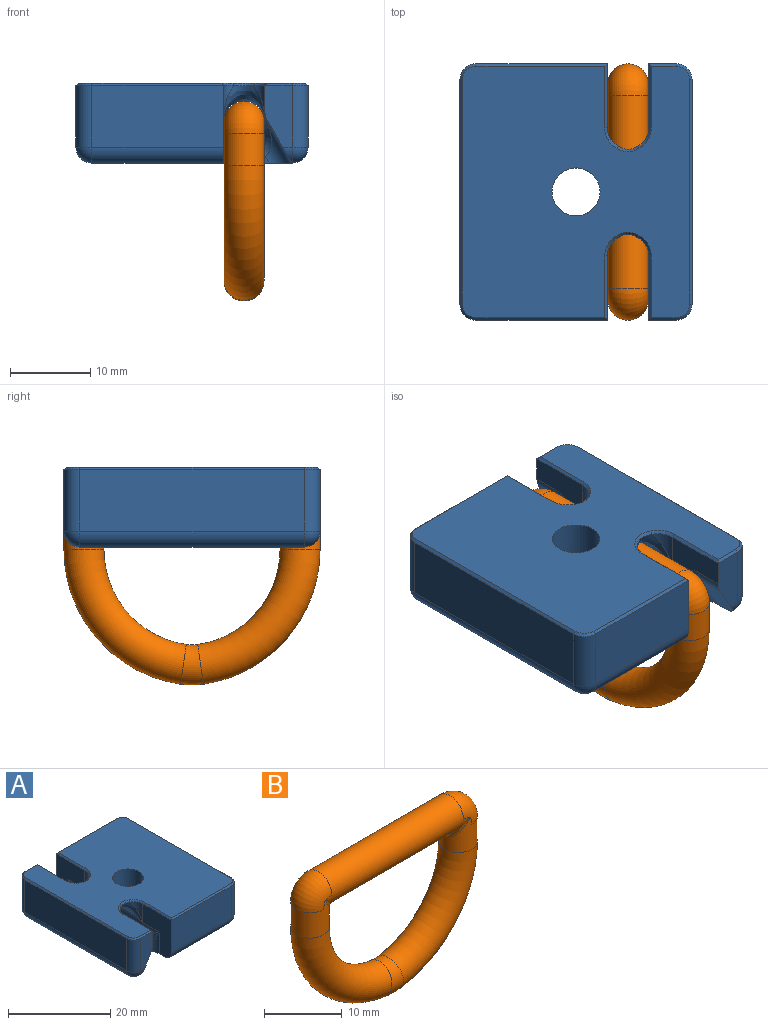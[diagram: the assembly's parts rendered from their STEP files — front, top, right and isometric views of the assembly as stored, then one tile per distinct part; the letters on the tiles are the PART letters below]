
ASSEMBLY  parts=2 mates=1
PART A: 73 faces, bbox 29.6x32.6x13.1 mm
  f0: cylinder r=2.6mm len=4.5mm, axis (0,0,1), area 6.3mm2, adj f31,f52,f54
  f1: cylinder r=2.6mm len=4.5mm, axis (0,0,1), area 6.3mm2, adj f27,f51,f71
  f2: cylinder r=2.6mm len=25mm, axis (0,-1,0), area 221.5mm2, adj f25,f27,f30,f31,f41,f42,f43,f46
  f3: plane 31.46x28.46mm, normal (0,0,1), area 745mm2, adj f33,f53,f54,f55,f56,f57,f58,f59
  f4: plane 16.4x7.7mm, normal (0,-1,0), area 126.3mm2, adj f17,f18,f30,f62
  f5: cylinder r=2mm len=1.99mm, axis (1,0,0), area 1.7mm2, adj f12,f14,f32
  f6: plane 16.4x7.7mm, normal (0,1,0), area 126.3mm2, adj f9,f24,f27,f70
  f7: plane 7.7x3.4mm, normal (0,1,0), area 21.8mm2, adj f15,f21,f25,f28,f45,f63
  f8: plane 28.61x25.61mm, normal (0,0,-1), area 558.4mm2, adj f9,f16,f17,f22,f26,f27,f29,f30
  f9: cylinder r=2mm len=16.4mm, axis (-1,0,0), area 51.5mm2, adj f6,f8,f23,f27
  f10: plane 28x7.7mm, normal (1,0,0), area 215.6mm2, adj f18,f22,f24,f66
  f11: plane 28x7.7mm, normal (-1,0,0), area 215.6mm2, adj f13,f15,f16,f59
  f12: plane 7.7x3.4mm, normal (0,-1,0), area 21.8mm2, adj f5,f13,f31,f32,f50,f55
  f13: cylinder r=2mm len=7.7mm, axis (0,0,1), area 24.2mm2, adj f11,f12,f14,f57
  f14: sphere r=2mm, area 6.3mm2, adj f5,f13,f16,f32
  f15: cylinder r=2mm len=7.7mm, axis (0,0,-1), area 24.2mm2, adj f7,f11,f19,f61
  f16: cylinder r=2mm len=28mm, axis (0,-1,0), area 88mm2, adj f8,f11,f14,f19,f28,f32
  f17: cylinder r=2mm len=16.4mm, axis (1,0,0), area 51.5mm2, adj f4,f8,f20,f30
  f18: cylinder r=2mm len=7.7mm, axis (0,0,-1), area 24.2mm2, adj f4,f10,f20,f64
  f19: sphere r=2mm, area 6.3mm2, adj f15,f16,f21,f28
  f20: sphere r=2mm, area 8.6mm2, adj f17,f18,f22
  f21: cylinder r=2mm len=1.99mm, axis (-1,0,0), area 1.7mm2, adj f7,f19,f28
  f22: cylinder r=2mm len=28mm, axis (0,1,0), area 88mm2, adj f8,f10,f20,f23
  f23: sphere r=2mm, area 4mm2, adj f9,f22,f24
  f24: cylinder r=2mm len=7.7mm, axis (0,0,1), area 24.2mm2, adj f6,f10,f23,f68
  f25: plane 8x4.5mm, normal (1,0,0), area 28.9mm2, adj f2,f7,f36,f44,f45,f65
  f26: plane 3.22x0.83mm, normal (0,1,0), area 1.1mm2, adj f8,f39,f40,f42
  f27: plane 9.7x8mm, normal (-1,0,0), area 53.3mm2, adj f1,f2,f6,f8,f9,f39,f72
  f28: plane 5.73x3.92mm, normal (0.87,0,-0.5), area 20.5mm2, adj f7,f16,f19,f21,f40,f45
  f29: plane 3.22x0.83mm, normal (0,-1,0), area 1.1mm2, adj f8,f37,f38,f47
  f30: plane 9.7x8mm, normal (-1,0,0), area 53.3mm2, adj f2,f4,f8,f17,f35,f37,f60
  f31: plane 8x4.5mm, normal (1,0,0), area 28.9mm2, adj f0,f2,f12,f49,f50,f53
  f32: plane 5.73x3.92mm, normal (0.87,0,-0.5), area 20.5mm2, adj f5,f12,f14,f16,f38,f50
  f33: cylinder r=3mm len=8mm, axis (0,0,-1), area 150.8mm2, adj f3,f34
  f34: cone r=3mm half-angle=45deg, axis (0,0,-1), area 71.1mm2, adj f8,f33
  f35: cylinder r=2.6mm len=4.5mm, axis (0,0,1), area 6.3mm2, adj f30,f52,f58
  f36: cylinder r=2.6mm len=4.5mm, axis (0,0,1), area 6.3mm2, adj f25,f51,f67
  f37: cylinder r=2.5mm len=5.2mm, axis (0,0,-1), area 7.7mm2, adj f8,f29,f30,f46
  f38: cylinder r=2.5mm len=6.57mm, axis (0.5,0,0.87), area 14.1mm2, adj f8,f29,f32,f48,f49
  f39: cylinder r=2.5mm len=5.2mm, axis (0,0,-1), area 7.7mm2, adj f8,f26,f27,f41
  f40: cylinder r=2.5mm len=6.57mm, axis (0.5,0,0.87), area 14.1mm2, adj f8,f26,f28,f43,f44
  f41: bspline ~5.1x5mm, area 7.2mm2, adj f2,f39,f42
  f42: torus R=5.1mm, axis (0,-1,0), area 7.8mm2, adj f2,f26,f41,f43
  f43: bspline ~5.32x4.45mm, area 9.5mm2, adj f2,f40,f42,f44
  f44: bspline ~2.52x2.45mm, area 3.5mm2, adj f25,f40,f43,f45
  f45: cylinder r=2.5mm len=3.5mm, axis (0,1,0), area 4.6mm2, adj f7,f25,f28,f44
  f46: bspline ~5.1x5mm, area 7.2mm2, adj f2,f37,f47
  f47: torus R=5.1mm, axis (0,-1,0), area 7.8mm2, adj f2,f29,f46,f48
  f48: bspline ~4.74x3.91mm, area 9.5mm2, adj f2,f38,f47,f49
  f49: bspline ~2.52x2.45mm, area 3.5mm2, adj f31,f38,f48,f50
  f50: cylinder r=2.5mm len=3.5mm, axis (0,-1,0), area 4.6mm2, adj f12,f31,f32,f49
  f51: bspline ~5.2x5.1mm, area 21.3mm2, adj f1,f2,f36,f69
  f52: bspline ~5.2x5.1mm, area 21.5mm2, adj f0,f2,f35,f56
  f53: plane 8x0.3mm, normal (0.71,0,0.71), area 3.3mm2, adj f3,f31,f54,f55
  f54: cone r=2.6mm half-angle=45deg, axis (0,0,1), area 1.3mm2, adj f0,f3,f53,f56
  f55: plane 3.4x0.3mm, normal (0,-0.71,0.71), area 1.4mm2, adj f3,f12,f53,f57
  f56: bspline ~2.73x0.69mm, area 1.3mm2, adj f3,f52,f54,f58
  f57: cone r=1.7mm half-angle=45deg, axis (0,0,-1), area 1.2mm2, adj f3,f13,f55,f59
  f58: cone r=2.6mm half-angle=45deg, axis (0,0,1), area 1.3mm2, adj f3,f35,f56,f60
  f59: plane 28x0.3mm, normal (-0.71,0,0.71), area 11.9mm2, adj f3,f11,f57,f61
  f60: plane 8x0.3mm, normal (-0.71,0,0.71), area 3.3mm2, adj f3,f30,f58,f62
  f61: cone r=1.7mm half-angle=45deg, axis (0,0,-1), area 1.2mm2, adj f3,f15,f59,f63
  f62: plane 16.4x0.3mm, normal (0,-0.71,0.71), area 6.9mm2, adj f3,f4,f60,f64
  f63: plane 3.4x0.3mm, normal (0,0.71,0.71), area 1.4mm2, adj f3,f7,f61,f65
  f64: cone r=1.7mm half-angle=45deg, axis (0,0,-1), area 1.2mm2, adj f3,f18,f62,f66
  f65: plane 8x0.3mm, normal (0.71,0,0.71), area 3.3mm2, adj f3,f25,f63,f67
  f66: plane 28x0.3mm, normal (0.71,0,0.71), area 11.9mm2, adj f3,f10,f64,f68
  f67: cone r=2.6mm half-angle=45deg, axis (0,0,1), area 1.3mm2, adj f3,f36,f65,f69
  f68: cone r=1.7mm half-angle=45deg, axis (0,0,-1), area 1.2mm2, adj f3,f24,f66,f70
  f69: bspline ~2.73x0.69mm, area 1.3mm2, adj f3,f51,f67,f71
  f70: plane 16.4x0.3mm, normal (0,0.71,0.71), area 6.9mm2, adj f3,f6,f68,f72
  f71: cone r=2.6mm half-angle=45deg, axis (0,0,1), area 1.3mm2, adj f1,f3,f69,f72
  f72: plane 8x0.3mm, normal (-0.71,0,0.71), area 3.3mm2, adj f3,f27,f70,f71
PART B: 10 faces, bbox 34.8x5x26.2 mm
  f0: cylinder r=2.5mm len=26.35mm, axis (-1,0,0), area 365mm2, adj f6,f7,f8,f9
  f1: cylinder r=2.5mm len=5.18mm, axis (0,0,-1), area 56.9mm2, adj f3,f6,f8
  f2: cylinder r=2.5mm len=5.18mm, axis (0,0,1), area 56.9mm2, adj f4,f7,f9
  f3: torus R=14.5mm, axis (0,-1,0), area 325.1mm2, adj f1,f5
  f4: torus R=14.5mm, axis (0,-1,0), area 325.1mm2, adj f2,f5
  f5: torus R=7.5mm, axis (0,-1,0), area 33.8mm2, adj f3,f4
  f6: bspline ~5x3.5mm, area 8.9mm2, adj f0,f1,f8
  f7: bspline ~5x3.5mm, area 8.9mm2, adj f0,f2,f9
  f8: torus R=1.5mm, axis (0,-1,0), area 37.7mm2, adj f0,f1,f6
  f9: torus R=1.5mm, axis (0,-1,0), area 37.7mm2, adj f0,f2,f7
PLACE A rot(axis=(0,0,1),180deg) t=(0,0,-10)mm
PLACE B rot(axis=(0,0,1),90deg) t=(6.5,0,-14.8)mm
MATE revolute B.f0 <-> A.f2  axis (0,-1,0) through (6.5,0,-4.8)mm
